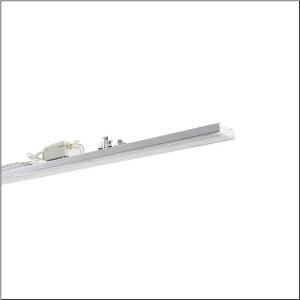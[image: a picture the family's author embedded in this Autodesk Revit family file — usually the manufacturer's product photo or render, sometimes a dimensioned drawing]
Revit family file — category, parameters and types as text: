
# Revit family: licross_r__21_recessed_mo_52te14dn49xg_1976
name_source: partatom
category: Lighting Fixtures
units: mm (PartAtom-declared; Revit-internal decimal feet)

## family parameters
Cut with Voids When Loaded = No
Host = Face
Light Source = No
Part Type = Normal
Room Calculation Point = No
Round Connector Dimension = Use Diameter
Shared = No

## types (1)
- --- (1 x LED, 9470 lm, 58 W, 4000K)
    Apparent Load = 58 VA
    CIE Flux Codes = 56 84 97 100 100
    Color Rendering = 80
    Color Temperature = 4000K
    Default Elevation = 1800 mm
    Description = Licross® 21 Recessed MO, luminaire insert, of sheet steel, galvanised, coil coated, white, length: 1.500mm, width: 66mm, height: 67mm, LED rated luminous flux: 9.470lm, light colour: 840, SDCM (Standard Deviation of Colour Matching)MacAdam ≤ 3 SDCM (initial), control gear: DALI 2, with plug, 5-pole, with phase selection, mains connection: 220..240V, AC, 50/60Hz, rated input power: 58W, internal wiring halogen-free, primary light control with lens, of plastic, primary optical cover: cover, of PMMA, light emission: direct distribution, primary light characteristic: asymmetric, protection rating (complete): IP54, insulation class (complete): insulation class I (protective earthing), certification: CE, ENEC, VDE, UKCA, protection symbol: D if used in an environment with non-conductive dust loads with corresponding accessories, impact resistance: IK06, permissible ambient temperature for indoor applications: -25..+35°C, corresponds to IFS (International Featured Standards) requirements for safety and quality in the food industry, reducing of maximum allowable ambient temperature of 5°C with ceiling mounting, LABS conformity tested according to VDMA 24364:2018-05, packaging unit: 1 piece
    Height = 58 mm
    Lamp = 1 x LED
    Lamp Light Flux = 9470 lm
    Lamp Power = 58 W
    Lamp count = 1
    Length = 1500 mm
    Luminous efficacy = 163 lm/W
    Manufacturer = Siteco
    ModVariant = No
    Model = 52TE14DN49XG
    Mounting Place = Ceiling
    Mounting Type = Pendant
    Number of Poles = 1
    OnlyDefault = Yes
    Power Factor = 1
    Product Name = Licross® 21 Recessed MO
    Product group = luminaire insert | ceiling pendant
    ProductGroupID = 901
    Protection Class = Protection class I
    Protection Degree = IP 54
    RLX_Detail_Level = 1
    RLX_Emergency_Light_Flux = 0 lm
    RLX_Emergency_Type = 0
    RLX_Emergency_Type_DB = No
    RlxData = <blob elided: 25145 chars, md5=f3d50355>
    Socket = socket
    Standby Power = 0 W
    System Light Flux = 9470 lm
    System Power = 58 W
    Type Comments = factory setting: luminous flux: 100 % | dim-lin: 254 | 390 mA
    Type Image = l_1296930.jpg
    URL = http://relux.com
    VarID = @adj_131665
    Voltage = 0 V
    Weight = 0.00 kg
    Width = 66 mm

## geometry (parser evidence)
native form markers: Blend x4, Sweep x12
no freeform markers — native parametric forms only
